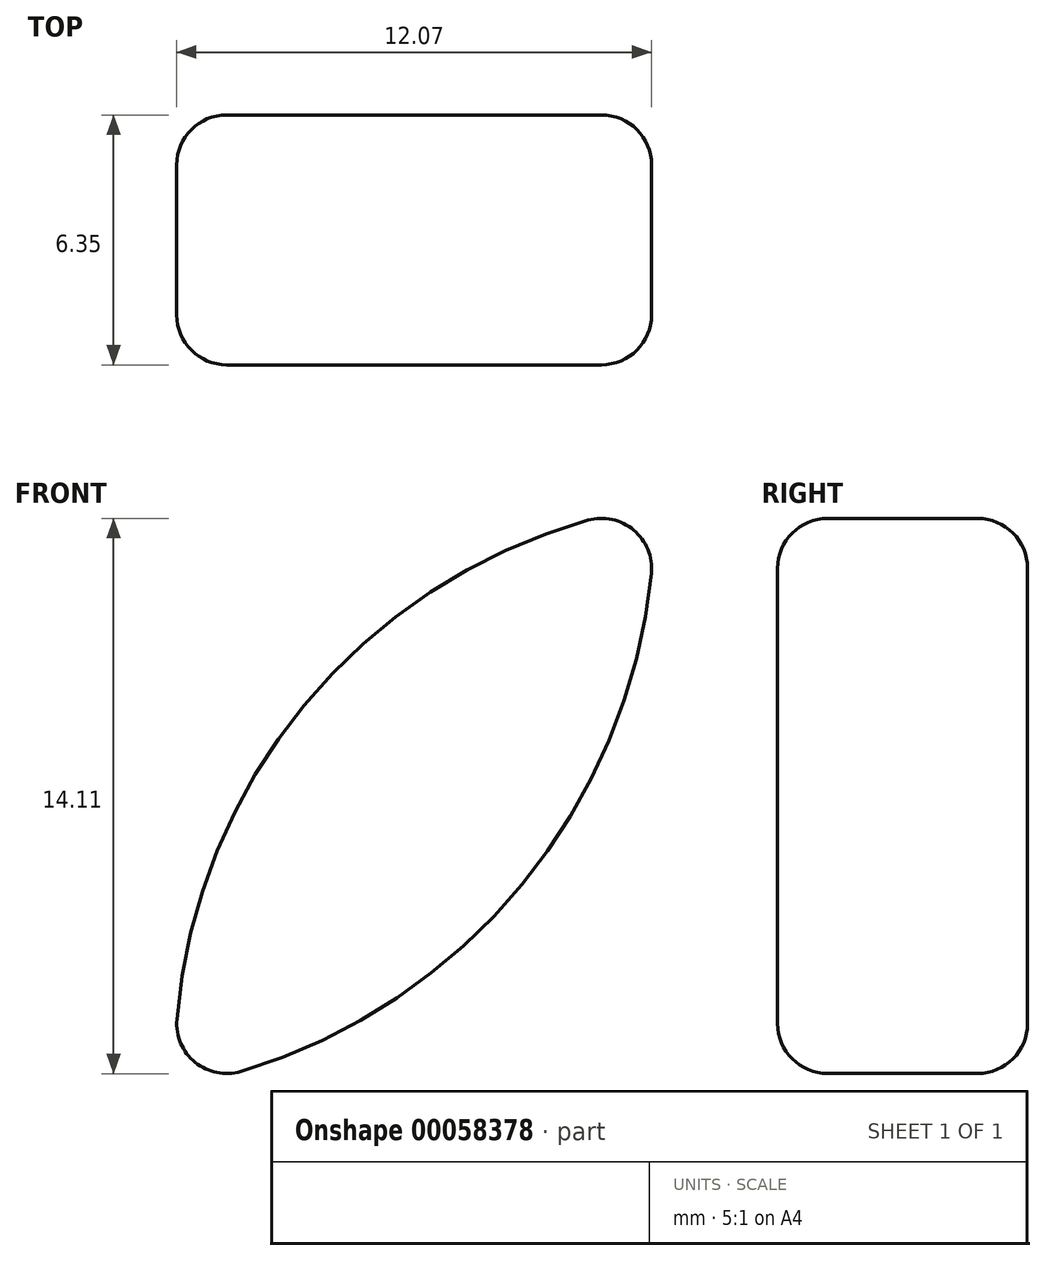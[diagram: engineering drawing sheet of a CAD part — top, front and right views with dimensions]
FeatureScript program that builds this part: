
annotation { "Feature Type Name" : "Feature", "Feature Type Description" : "" }
export const myFeature = defineFeature(function(context is Context, id is Id, definition is map)
    precondition{}
    {
        {
            var Q0;
            Q0=qCreatedBy(makeId("Front.planeOp"),FACE);
            var sketch = newSketch(context, id + "F0", { "sketchPlane" : qUnion([Q0])});
            skArc(sketch, "E0", {"start": v(12.16, 14.77) * mm, "mid": v(3.27, 9.7) * mm, "end": v(0, 0) * mm});
            skArc(sketch, "E1", {"start": v(0, 0) * mm, "mid": v(8.8, 5.14) * mm, "end": v(12.16, 14.77) * mm});
            skSolve(sketch);
        }
        {
            var Q0;
            Q0=makeQuery(id+"F0.imprint","IMPRINT",FACE,{"disambiguationData":[TD([[makeQuery(id+"F0.imprint","IMPRINT",EDGE,{"derivedFrom":sQuery(id+"F0.wireOp",EDGE,"E0")}),1.0]])]});
            extrude(context, id + "F1", {"entities" : qUnion([Q0]), "depth" : 6.35 * mm});
        }
        {
            var Q0;
            Q0=makeQuery(id+"F1.opExtrude","CAP_EDGE",EDGE,{"disambiguationData":[OSD([sQuery(id+"F0.wireOp",EDGE,"E0")])],"isStart":false});
            var Q1;
            Q1=makeQuery(id+"F1.opExtrude","CAP_EDGE",EDGE,{"disambiguationData":[OSD([sQuery(id+"F0.wireOp",EDGE,"E1")])],"isStart":false});
            var Q2;
            {var subQ0=sQuery(id+"F0.wireOp",EDGE,"E1");var subQ1=sQuery(id+"F0.wireOp",EDGE,"E0");Q2=makeQuery(id+"F1.opExtrude","SWEPT_EDGE",EDGE,{"disambiguationData":[OSD([subQ1,subQ0]),TDD([makeQuery(id+"F0.imprint","INTERSECT",VERTEX,{"disambiguationData":[OD(0.0)],"derivedFrom":[subQ1,subQ0]})])]});}
            var Q3;
            {var subQ0=sQuery(id+"F0.wireOp",EDGE,"E1");var subQ1=sQuery(id+"F0.wireOp",EDGE,"E0");Q3=makeQuery(id+"F1.opExtrude","SWEPT_EDGE",EDGE,{"disambiguationData":[OSD([subQ1,subQ0]),TDD([makeQuery(id+"F0.imprint","INTERSECT",VERTEX,{"disambiguationData":[OD(1.0)],"derivedFrom":[subQ1,subQ0]})])]});}
            fillet(context, id + "F2", {"entities" : qUnion([Q0, Q1, Q2, Q3]), "radius" : 1.27 * mm, "tangentPropagation" : true, "allowEdgeOverflow" : false});
        }
        {
            var Q0;
            Q0=makeQuery(id+"F1.opExtrude","CAP_EDGE",EDGE,{"disambiguationData":[OSD([sQuery(id+"F0.wireOp",EDGE,"E0")])],"isStart":true});
            var Q1;
            Q1=makeQuery(id+"F1.opExtrude","CAP_EDGE",EDGE,{"disambiguationData":[OSD([sQuery(id+"F0.wireOp",EDGE,"E1")])],"isStart":true});
            fillet(context, id + "F3", {"entities" : qUnion([Q0, Q1]), "radius" : 1.27 * mm, "tangentPropagation" : true, "allowEdgeOverflow" : false});
        }
    });
